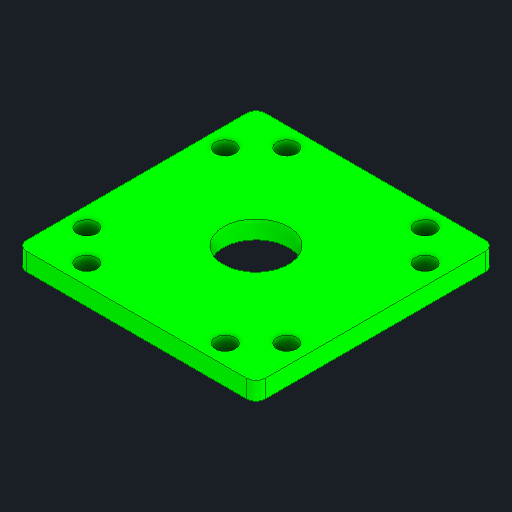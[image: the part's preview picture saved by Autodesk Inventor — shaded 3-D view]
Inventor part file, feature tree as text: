
AUTODESK INVENTOR PART (.ipt)
format: ipt  version: 2023.4 (Build 274418000, 418)  size: 212,992 bytes
history: native  units: mm
features: other x3, extrude x1, reference x1
ambient origin geometry x8: Origin, YZ Plane, XZ Plane, XY Plane, X Axis, Y Axis, Z Axis, Center Point
bodies: Solid1 (feature_tree)
feature tree (5):
  extrude  "Extrusion1"  Depth=3.75mm TaperAngle=0.0deg
  reference  "Reference1"
  parser-record x1  (decoder bookkeeping rows leaked as tree rows — omitted from the tree; the rows remain in map.json)
  other  "Cube 1x1 V5.iam"
  other  "Cube 1x1 Top V5:1"
note: 1 file-system path scrubbed to <path> (originals preserved in map.json)
